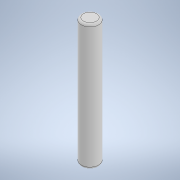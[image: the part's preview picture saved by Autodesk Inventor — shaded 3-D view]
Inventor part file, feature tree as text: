
AUTODESK INVENTOR PART (.ipt)
format: ipt  version: 2022 (Build 260153000, 153)  size: 103,936 bytes
history: native  units: mm
features: fillet x2, other x1, extrude x1, sketch x1
ambient origin geometry x8: Origin, YZ Plane, XZ Plane, XY Plane, X Axis, Y Axis, Z Axis, Center Point
bodies: Body1 (feature_tree)
feature tree (5):
  other  "ソリッド1"
  extrude  "押し出し1"  Depth=4.0mm
  fillet  "フィレット1"  Radius=29.0mm
  fillet  "フィレット2"  Radius=0.5mm
  sketch  "スケッチ1"
